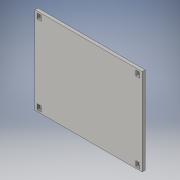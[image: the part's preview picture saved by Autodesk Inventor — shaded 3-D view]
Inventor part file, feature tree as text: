
AUTODESK INVENTOR PART (.ipt)
format: ipt  version: 2016 (Build 200138000, 138)  size: 103,424 bytes
history: native  units: in
note: dims shown in document units (in); Inventor stores cm internally (conversion verified against a paired STEP export)
features: extrude x1, sketch x1
ambient origin geometry x8: Origin, YZ Plane, XZ Plane, XY Plane, X Axis, Y Axis, Z Axis, Center Point
bodies: Solid1 (feature_tree)
feature tree (2):
  extrude  "Extrusion1"  [1 undecoded]
  sketch  "Sketch1"  dims[d2=0.09in d3=0.0in]
note: 1 required parameter value undecoded (feature->parameter linkage not recoverable at this tier; creation-order binding heuristic only, values carry confidence <= 0.55)
